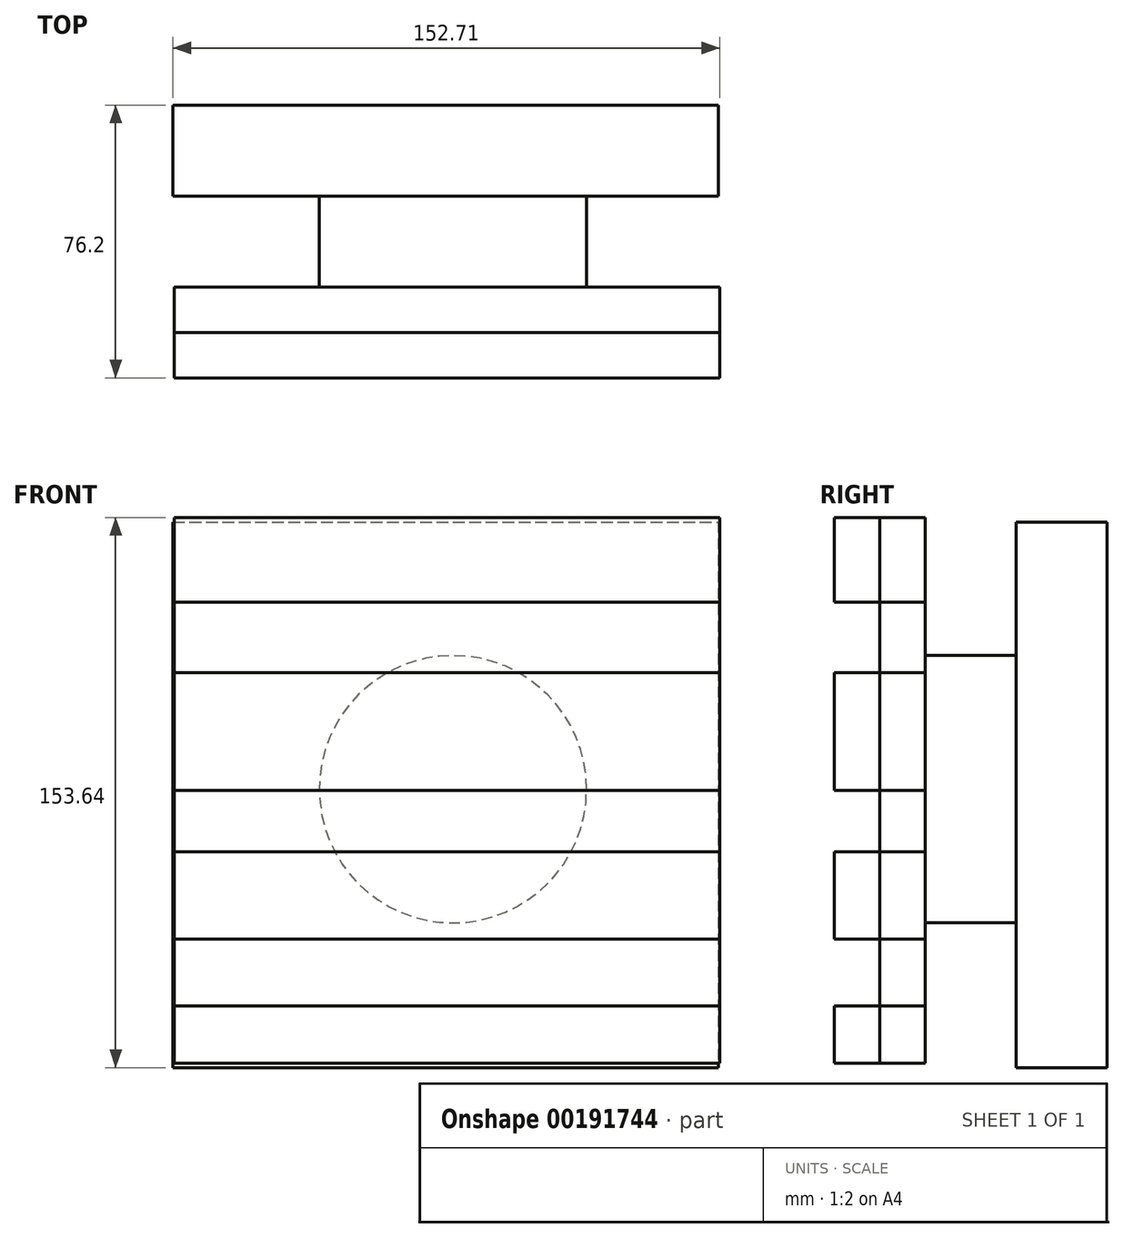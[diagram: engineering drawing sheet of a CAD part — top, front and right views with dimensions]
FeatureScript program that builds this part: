
annotation { "Feature Type Name" : "Feature", "Feature Type Description" : "" }
export const myFeature = defineFeature(function(context is Context, id is Id, definition is map)
    precondition{}
    {
        {
            var Q0;
            Q0=qCreatedBy(makeId("Front.planeOp"),FACE);
            var sketch = newSketch(context, id + "F0", { "sketchPlane" : qUnion([Q0])});
            skLineSegment(sketch, "E0.bottom", {"start": v(-90.95, 86.57) * mm, "end": v(61.45, 86.57) * mm});
            skLineSegment(sketch, "E0.top", {"start": v(-90.95, -65.83) * mm, "end": v(61.45, -65.83) * mm});
            skLineSegment(sketch, "E0.left", {"start": v(-90.95, 86.57) * mm, "end": v(-90.95, -65.83) * mm});
            skLineSegment(sketch, "E0.right", {"start": v(61.45, 86.57) * mm, "end": v(61.45, -65.83) * mm});
            skLineSegment(sketch, "E1.bottom", {"start": v(61.45, -49.83) * mm, "end": v(-90.95, -49.83) * mm});
            skLineSegment(sketch, "E1.top", {"start": v(61.45, -31.12) * mm, "end": v(-90.95, -31.12) * mm});
            skLineSegment(sketch, "E1.left", {"start": v(61.45, -49.83) * mm, "end": v(61.45, -31.12) * mm});
            skLineSegment(sketch, "E1.right", {"start": v(-90.95, -49.83) * mm, "end": v(-90.95, -31.12) * mm});
            skLineSegment(sketch, "E2.bottom", {"start": v(61.45, -6.83) * mm, "end": v(-90.95, -6.83) * mm});
            skLineSegment(sketch, "E2.top", {"start": v(61.45, 10.37) * mm, "end": v(-90.95, 10.37) * mm});
            skLineSegment(sketch, "E2.left", {"start": v(61.45, -6.83) * mm, "end": v(61.45, 10.37) * mm});
            skLineSegment(sketch, "E2.right", {"start": v(-90.95, -6.83) * mm, "end": v(-90.95, 10.37) * mm});
            skLineSegment(sketch, "E3.bottom", {"start": v(61.45, 43.25) * mm, "end": v(-90.95, 43.25) * mm});
            skLineSegment(sketch, "E3.top", {"start": v(61.45, 62.98) * mm, "end": v(-90.95, 62.98) * mm});
            skLineSegment(sketch, "E3.left", {"start": v(61.45, 43.25) * mm, "end": v(61.45, 62.98) * mm});
            skLineSegment(sketch, "E3.right", {"start": v(-90.95, 43.25) * mm, "end": v(-90.95, 62.98) * mm});
            skSolve(sketch);
        }
        {
            var Q0;
            {var subQ0=sQuery(id+"F0.wireOp",EDGE,"E0.bottom");Q0=makeQuery(id+"F0.imprint","IMPRINT",FACE,{"disambiguationData":[TD([[makeQuery(id+"F0.imprint","IMPRINT",EDGE,{"derivedFrom":subQ0}),-1.0]])]});}
            var Q1;
            {var subQ0=sQuery(id+"F0.wireOp",EDGE,"E0.top");Q1=makeQuery(id+"F0.imprint","IMPRINT",FACE,{"disambiguationData":[TD([[makeQuery(id+"F0.imprint","IMPRINT",EDGE,{"derivedFrom":subQ0}),1.0]])]});}
            var Q2;
            {var subQ0=sQuery(id+"F0.wireOp",EDGE,"E2.top");Q2=makeQuery(id+"F0.imprint","IMPRINT",FACE,{"disambiguationData":[TD([[makeQuery(id+"F0.imprint","IMPRINT",EDGE,{"derivedFrom":subQ0}),-1.0]])]});}
            var Q3;
            {var subQ0=sQuery(id+"F0.wireOp",EDGE,"E1.top");Q3=makeQuery(id+"F0.imprint","IMPRINT",FACE,{"disambiguationData":[TD([[makeQuery(id+"F0.imprint","IMPRINT",EDGE,{"derivedFrom":subQ0}),-1.0]])]});}
            extrude(context, id + "F1", {"entities" : qUnion([Q0, Q1, Q2, Q3]), "depth" : 25.4 * mm});
        }
        {
            var Q0;
            Q0 = qSketchRegion(id + "F0", true);
            extrude(context, id + "F2", {"entities" : qUnion([Q0]), "depth" : 12.7 * mm});
        }
        {
            var Q0;
            Q0=qCreatedBy(makeId("Front.planeOp"),FACE);
            var sketch = newSketch(context, id + "F3", { "sketchPlane" : qUnion([Q0])});
            skCircle(sketch, "E4", {"center": v(-13.04, 10.69) * mm, "radius": 37.33 * mm});
            skSolve(sketch);
        }
        {
            var Q0;
            Q0 = qSketchRegion(id + "F3", true);
            extrude(context, id + "F4", {"entities" : qUnion([Q0]), "oppositeDirection" : true, "depth" : 25.4 * mm});
        }
        {
            var Q0;
            Q0=makeQuery(id+"F4.opExtrude","CAP_FACE",FACE,{"disambiguationData":[OSD([sQuery(id+"F3.wireOp",EDGE,"E4")])],"isStart":false});
            var sketch = newSketch(context, id + "F5", { "sketchPlane" : qUnion([Q0])});
            skLineSegment(sketch, "E5.bottom", {"start": v(91.26, 85.33) * mm, "end": v(-61.14, 85.33) * mm});
            skLineSegment(sketch, "E5.top", {"start": v(91.26, -67.07) * mm, "end": v(-61.14, -67.07) * mm});
            skLineSegment(sketch, "E5.left", {"start": v(91.26, 85.33) * mm, "end": v(91.26, -67.07) * mm});
            skLineSegment(sketch, "E5.right", {"start": v(-61.14, 85.33) * mm, "end": v(-61.14, -67.07) * mm});
            skSolve(sketch);
        }
        {
            var Q0;
            Q0 = qSketchRegion(id + "F5", true);
            extrude(context, id + "F6", {"entities" : qUnion([Q0]), "operationType" : NewBodyOperationType.ADD, "depth" : 25.4 * mm});
        }
    });
